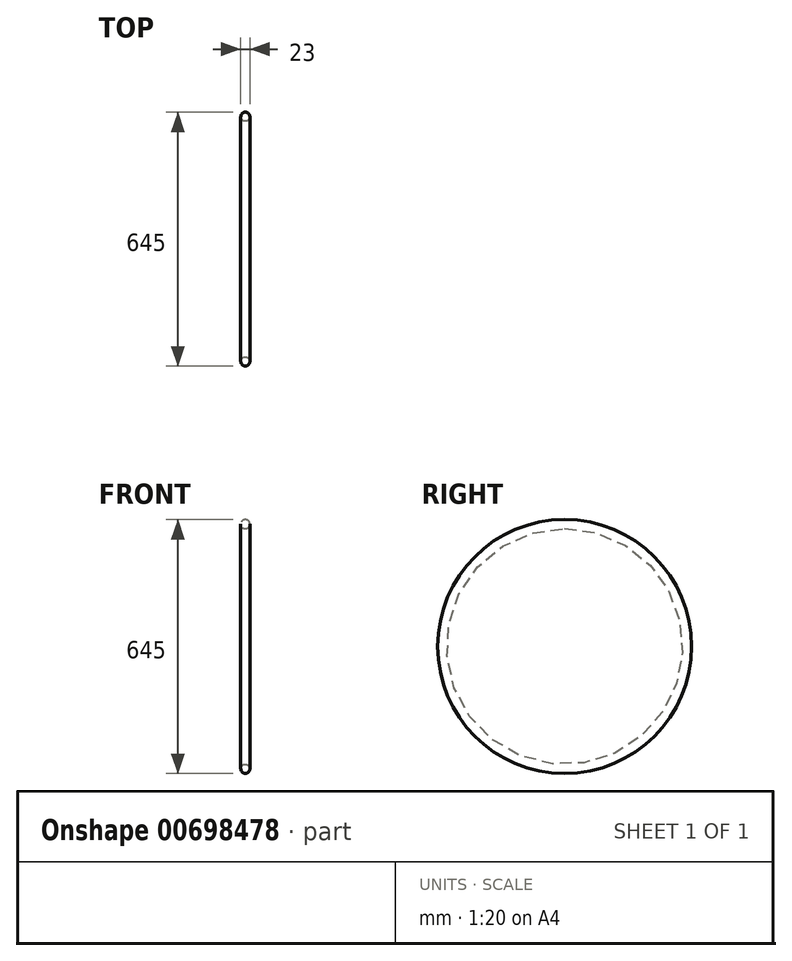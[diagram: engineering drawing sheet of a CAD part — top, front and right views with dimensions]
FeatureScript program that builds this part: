
annotation { "Feature Type Name" : "Feature", "Feature Type Description" : "" }
export const myFeature = defineFeature(function(context is Context, id is Id, definition is map)
    precondition{}
    {
        {
            var Q0;
            Q0=qCreatedBy(makeId("Front.planeOp"),FACE);
            var sketch = newSketch(context, id + "F0", { "sketchPlane" : qUnion([Q0])});
            skCircle(sketch, "E0", {"center": v(0, 0) * mm, "radius": 11.5 * mm});
            skLineSegment(sketch, "E1", {"start": v(0, -311) * mm, "end": v(0, 0) * mm});
            skLineSegment(sketch, "E2", {"start": v(0, -311) * mm, "end": v(37, -311) * mm});
            skSolve(sketch);
        }
        {
            var Q0;
            Q0=makeQuery(id+"F0.imprint","IMPRINT",FACE,{"disambiguationData":[TD([[makeQuery(id+"F0.imprint","IMPRINT",EDGE,{"derivedFrom":sQuery(id+"F0.wireOp",EDGE,"E0")}),1.0]])]});
            var Q1;
            Q1=sQuery(id+"F0.wireOp",EDGE,"E2");
            revolve(context, id + "F1", {"entities" : qUnion([Q0]), "axis" : qUnion([Q1]), "revolveType" : RevolveType.FULL});
        }
    });
